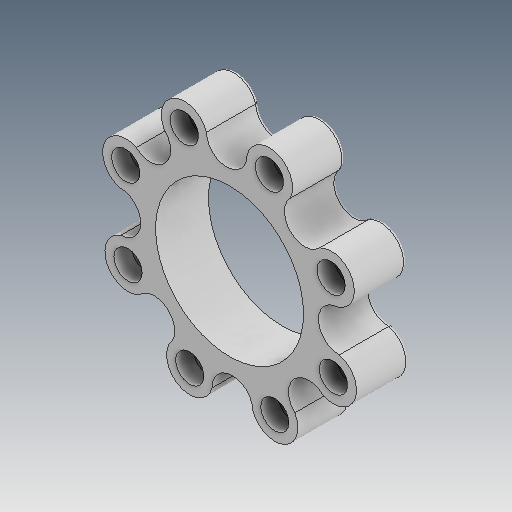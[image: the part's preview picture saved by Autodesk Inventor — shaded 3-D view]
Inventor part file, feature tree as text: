
AUTODESK INVENTOR PART (.ipt)
format: ipt  version: 2020.3 (Build 243373010, 373A)  size: 334,336 bytes
history: native  units: mm
features: sketch x5, extrude x3, fillet x1, hole x1, pattern_circular x1, projected_geometry x1
ambient origin geometry x8: Origin, YZ Plane, XZ Plane, XY Plane, X Axis, Y Axis, Z Axis, Center Point
bodies: Body1 (feature_tree)
feature tree (12):
  sketch  "Sketch1"  dims[d0=50.0mm d24=15.0mm d25=0.0mm]
  extrude  "Extrusion3"  Depth=15.0mm TaperAngle=0.0deg
  extrude  "Extrusion4"  Depth=1.919862mm
  fillet  "Fillet2"  Radius=4.18879mm
  extrude  "Extrusion5"  Depth=80.0mm TaperAngle=360.0deg
  sketch  "Sketch4"  dims[d39=80.0mm d41=360.0deg d43=80.0mm d45=360.0deg]
  hole  "Hole1"  [1 undecoded]
  pattern_circular  "Circular Pattern2"  [2 undecoded]
  sketch  "Sketch9"  dims[d50=42.0mm d51=0.0mm d52=0.0mm d57=5.0mm d58=10.0mm d59=8.0mm d60=5.0mm d61=90.0deg d62=10.0mm d63=20.594885mm d64=80.0mm d65=360.0deg d12=0.5mm d13=0.872665mm d14=0.5mm d15=0.872665mm]
  sketch  "Sketch3"  dims[d28=3.839724mm d29=2.094395mm d35=1.919862mm d36=4.18879mm]
  sketch  "Sketch8"  dims[d47=15.0mm d48=0.0mm d49=1.0mm]
  projected_geometry  "Projected Loop5"
note: 3 required parameter values undecoded (feature->parameter linkage not recoverable at this tier; creation-order binding heuristic only, values carry confidence <= 0.55)
